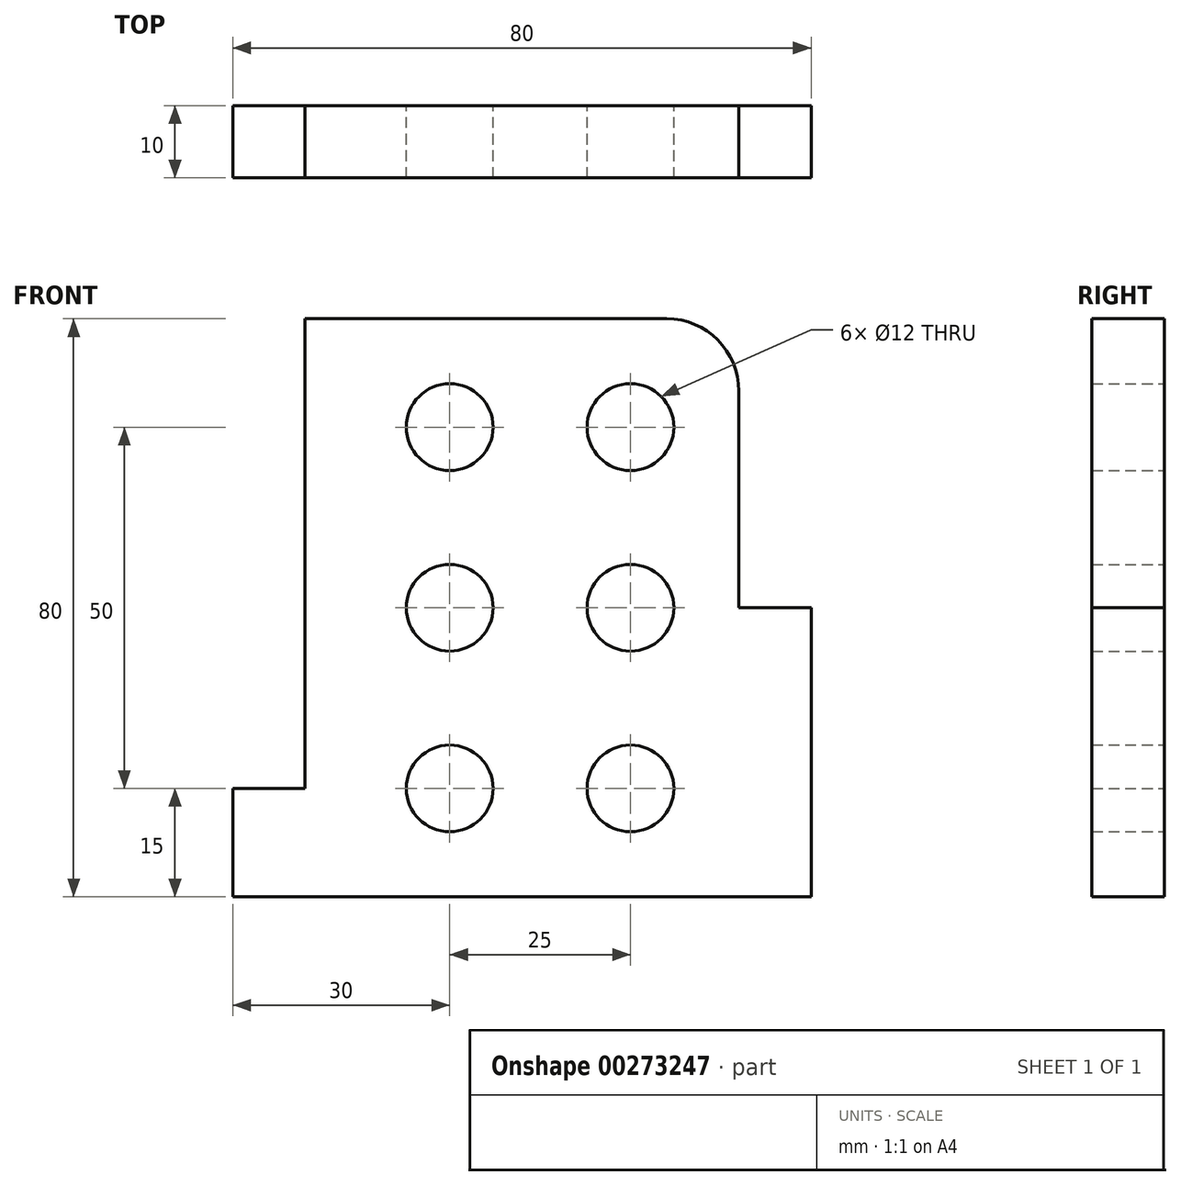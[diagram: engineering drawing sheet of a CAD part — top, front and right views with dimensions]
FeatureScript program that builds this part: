
annotation { "Feature Type Name" : "Feature", "Feature Type Description" : "" }
export const myFeature = defineFeature(function(context is Context, id is Id, definition is map)
    precondition{}
    {
        {
            var Q0;
            Q0=qCreatedBy(makeId("Front.planeOp"),FACE);
            var sketch = newSketch(context, id + "F0", { "sketchPlane" : qUnion([Q0])});
            skLineSegment(sketch, "E0", {"start": v(0, 0) * mm, "end": v(0, 15) * mm});
            skLineSegment(sketch, "E1", {"start": v(0, 15) * mm, "end": v(10, 15) * mm});
            skLineSegment(sketch, "E2", {"start": v(10, 80) * mm, "end": v(60, 80) * mm});
            skLineSegment(sketch, "E3", {"start": v(70, 70) * mm, "end": v(70, 40) * mm});
            skLineSegment(sketch, "E4", {"start": v(70, 40) * mm, "end": v(80, 40) * mm});
            skLineSegment(sketch, "E5", {"start": v(80, 40) * mm, "end": v(80, 0) * mm});
            skLineSegment(sketch, "E6", {"start": v(80, 0) * mm, "end": v(0, 0) * mm});
            skPoint(sketch, "E7.visualSharp", {"position": v(70, 80) * mm});
            skArc(sketch, "E7.filletArc", {"start": v(70, 70) * mm, "mid": v(67.07, 77.07) * mm, "end": v(60, 80) * mm});
            skCircle(sketch, "E8", {"center": v(30, 15) * mm, "radius": 6 * mm});
            skCircle(sketch, "E9", {"center": v(55, 15) * mm, "radius": 6 * mm});
            skCircle(sketch, "E10", {"center": v(30, 40) * mm, "radius": 6 * mm});
            skCircle(sketch, "E11", {"center": v(30, 65) * mm, "radius": 6 * mm});
            skCircle(sketch, "E12", {"center": v(55, 40) * mm, "radius": 6 * mm});
            skCircle(sketch, "E13", {"center": v(55, 65) * mm, "radius": 6 * mm});
            skLineSegment(sketch, "E14", {"start": v(10, 80) * mm, "end": v(10, 15) * mm});
            skSolve(sketch);
        }
        {
            var Q0;
            Q0=makeQuery(id+"F0.imprint","IMPRINT",FACE,{"disambiguationData":[TD([[makeQuery(id+"F0.imprint","IMPRINT",EDGE,{"derivedFrom":sQuery(id+"F0.wireOp",EDGE,"E0")}),-1.0]])]});
            extrude(context, id + "F1", {"entities" : qUnion([Q0]), "depth" : 10 * mm});
        }
    });
